# Revit family: Plumbing Fixture_Water Heater_Stiebel Eltron_SNU
name_source: partatom
category: Plumbing Fixtures
revit_build: Autodesk Revit 2015 (Build: 20140223_1515(x64)
units: mm (PartAtom-declared; Revit-internal decimal feet)

## types (2) — shared parameters
ApparentLoad_ANZRS = 2400 VA
Body Material = z_Stiebel Eltron_White
Button  Material = z_Stiebel Eltron_Black
CW Connection = Yes
HW Connection = Yes
Manufacturer = Stiebel Eltron
Manufacturer_URL__Product Specific = http://www.stiebel.com.au
Type Comments = Instantaneous Water Heater
URL = http://www.stiebel.com.au
Vent Connection = No
Waste Connection = No

## per-type parameters (varying)
| type | Description | Manufacturer_Overall Depth | Manufacturer_Overall Height | Manufacturer_Overall Width | Manufacturer_Spec Code | Model |
| 5 | Compact Under Sink Point of Use Water Heater - 5 Litre | 230 mm  [stored 0.754593 ft] | 421 mm  [stored 1.38123 ft] | 263 mm  [stored 0.862861 ft] | SNU 5 | SNU 5 |
| 10 | Compact Under Sink Point of Use Water Heater - 10 Litre | 275 mm | 503 mm | 295 mm | SNU 10 | SNU 10 |

note: [stored X ft] marks values corroborated as IEEE doubles in the binary element streams (Revit-internal decimal feet)

## geometry (parser evidence)
native form markers: Sweep x2
no freeform markers — native parametric forms only
